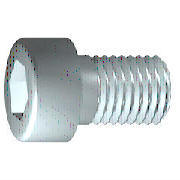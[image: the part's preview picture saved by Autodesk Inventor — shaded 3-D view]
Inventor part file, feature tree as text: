
AUTODESK INVENTOR PART (.ipt)
format: ipt  version: 2017 SP1 (Build 210196100, 196)  size: 188,928 bytes
history: native  units: mm (DEFAULTED — no unit token found)
features: sketch x2, extrude x1, plane x1, fillet x1
ambient origin geometry x7: Origin, YZ Plane, XY Plane, X Axis, Y Axis, Z Axis, Center Point
bodies: Solid1 (feature_tree), Body (feature_tree)
feature tree (5):
  extrude  "Slot"  Depth=6.0mm
  plane  "Work Plane1"
  fillet  "Fillet2"  Radius=6.0mm
  sketch  "Sketch1"  dims[d1=27.5mm d2=0.61355mm d3=6.0mm]
  sketch  "Sketch2"  dims[d4=3.0mm d5=60.0deg d6=6.0mm d7=6.0mm d8=5.773503mm d9=10.0mm d10=90.0deg d11=10.0mm d12=0.0mm d13=27.5mm d14=0.0mm d15=0.61345mm d16=0.61345mm d17=0.6mm d19=0.0mm d26=30.0mm d27=45.0deg d28=0.0mm d29=0.0mm d30=0.1mm]
